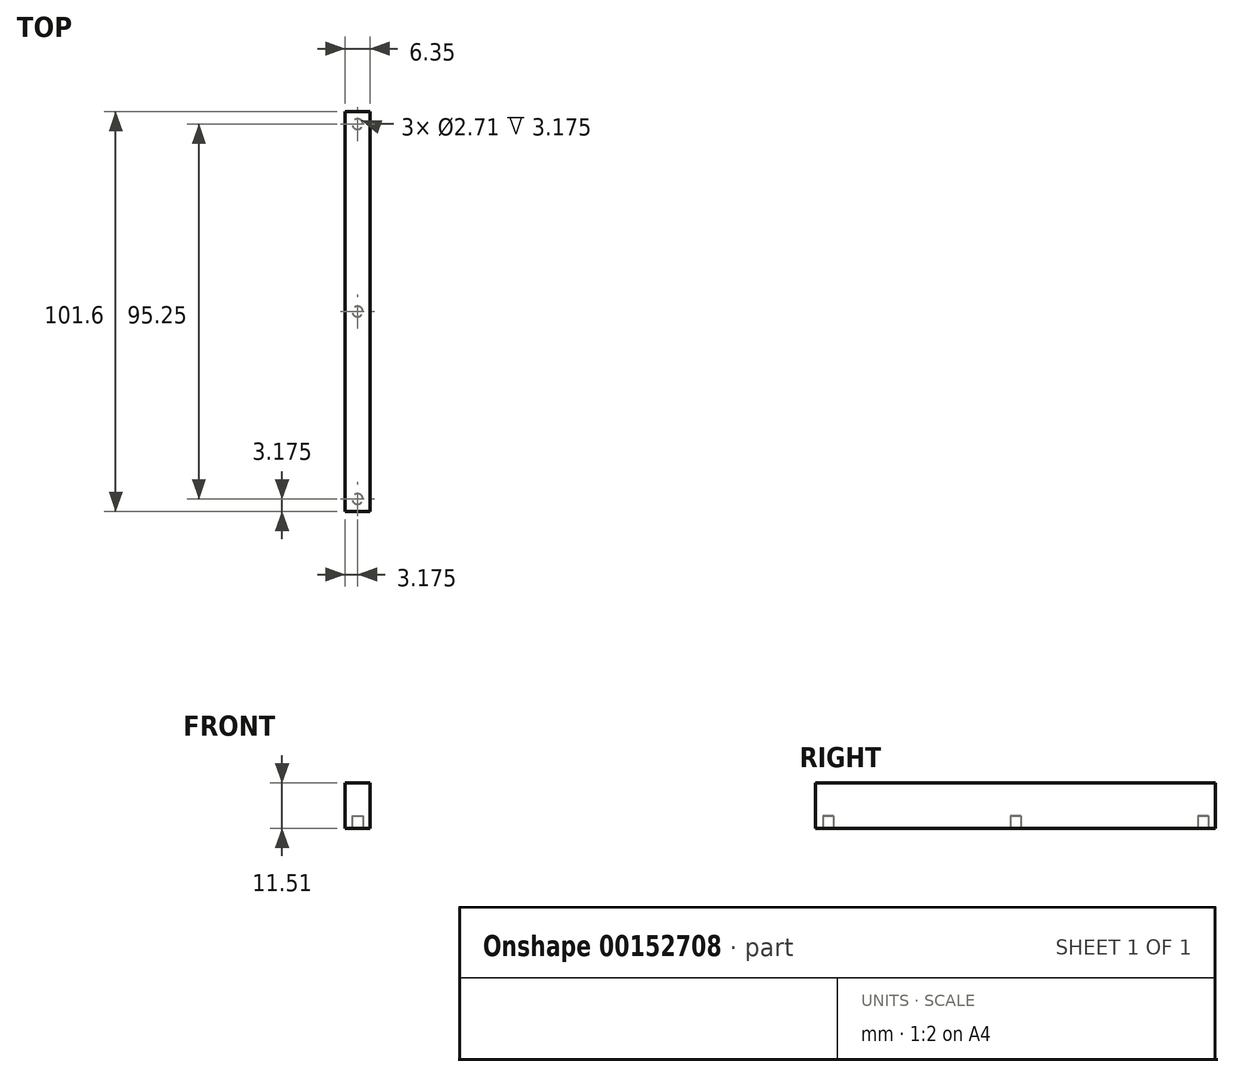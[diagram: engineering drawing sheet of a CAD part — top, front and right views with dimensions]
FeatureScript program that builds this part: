
annotation { "Feature Type Name" : "Feature", "Feature Type Description" : "" }
export const myFeature = defineFeature(function(context is Context, id is Id, definition is map)
    precondition{}
    {
        {
            var Q0;
            Q0=qCreatedBy(makeId("Top.planeOp"),FACE);
            var sketch = newSketch(context, id + "F0", { "sketchPlane" : qUnion([Q0])});
            skLineSegment(sketch, "E0.bottom", {"start": v(0, 0) * mm, "end": v(-6.35, 0) * mm});
            skLineSegment(sketch, "E0.top", {"start": v(0, -101.6) * mm, "end": v(-6.35, -101.6) * mm});
            skLineSegment(sketch, "E0.left", {"start": v(0, 0) * mm, "end": v(0, -101.6) * mm});
            skLineSegment(sketch, "E0.right", {"start": v(-6.35, 0) * mm, "end": v(-6.35, -101.6) * mm});
            skSolve(sketch);
        }
        {
            var Q0;
            Q0=qSketchRegion(id+"F0",true);
            extrude(context, id + "F1", {"entities" : qUnion([Q0]), "depth" : 11.5 * mm});
        }
        {
            var Q0;
            Q0=makeQuery(id+"F1.opExtrude","CAP_FACE",FACE,{"disambiguationData":[OSD([sQuery(id+"F0.wireOp",EDGE,"E0.bottom"),sQuery(id+"F0.wireOp",EDGE,"E0.top"),sQuery(id+"F0.wireOp",EDGE,"E0.left"),sQuery(id+"F0.wireOp",EDGE,"E0.right")])],"isStart":true});
            var sketch = newSketch(context, id + "F2", { "sketchPlane" : qUnion([Q0])});
            skLineSegment(sketch, "E1.bottom", {"start": v(-3.17, 101.6) * mm, "end": v(-6.35, 101.6) * mm, "construction": true});
            skLineSegment(sketch, "E1.top", {"start": v(-3.17, 98.43) * mm, "end": v(-6.35, 98.43) * mm, "construction": true});
            skLineSegment(sketch, "E1.left", {"start": v(-3.17, 101.6) * mm, "end": v(-3.17, 98.43) * mm, "construction": true});
            skLineSegment(sketch, "E1.right", {"start": v(-6.35, 101.6) * mm, "end": v(-6.35, 98.43) * mm, "construction": true});
            skLineSegment(sketch, "E2.bottom", {"start": v(-3.17, 0) * mm, "end": v(-6.35, 0) * mm, "construction": true});
            skLineSegment(sketch, "E2.top", {"start": v(-3.17, 3.17) * mm, "end": v(-6.35, 3.17) * mm, "construction": true});
            skLineSegment(sketch, "E2.left", {"start": v(-3.17, 0) * mm, "end": v(-3.17, 3.17) * mm, "construction": true});
            skLineSegment(sketch, "E2.right", {"start": v(-6.35, 0) * mm, "end": v(-6.35, 3.17) * mm, "construction": true});
            skLineSegment(sketch, "E3", {"start": v(-3.17, 98.43) * mm, "end": v(-3.17, 3.17) * mm, "construction": true});
            skCircle(sketch, "E4", {"center": v(-3.17, 98.43) * mm, "radius": 1.35 * mm});
            skCircle(sketch, "E5", {"center": v(-3.17, 50.8) * mm, "radius": 1.35 * mm});
            skCircle(sketch, "E6", {"center": v(-3.17, 3.17) * mm, "radius": 1.35 * mm});
            skSolve(sketch);
        }
        {
            var Q0;
            Q0=qSketchRegion(id+"F2",true);
            extrude(context, id + "F3", {"entities" : qUnion([Q0]), "operationType" : NewBodyOperationType.REMOVE, "oppositeDirection" : true, "depth" : 3.17 * mm});
        }
    });
